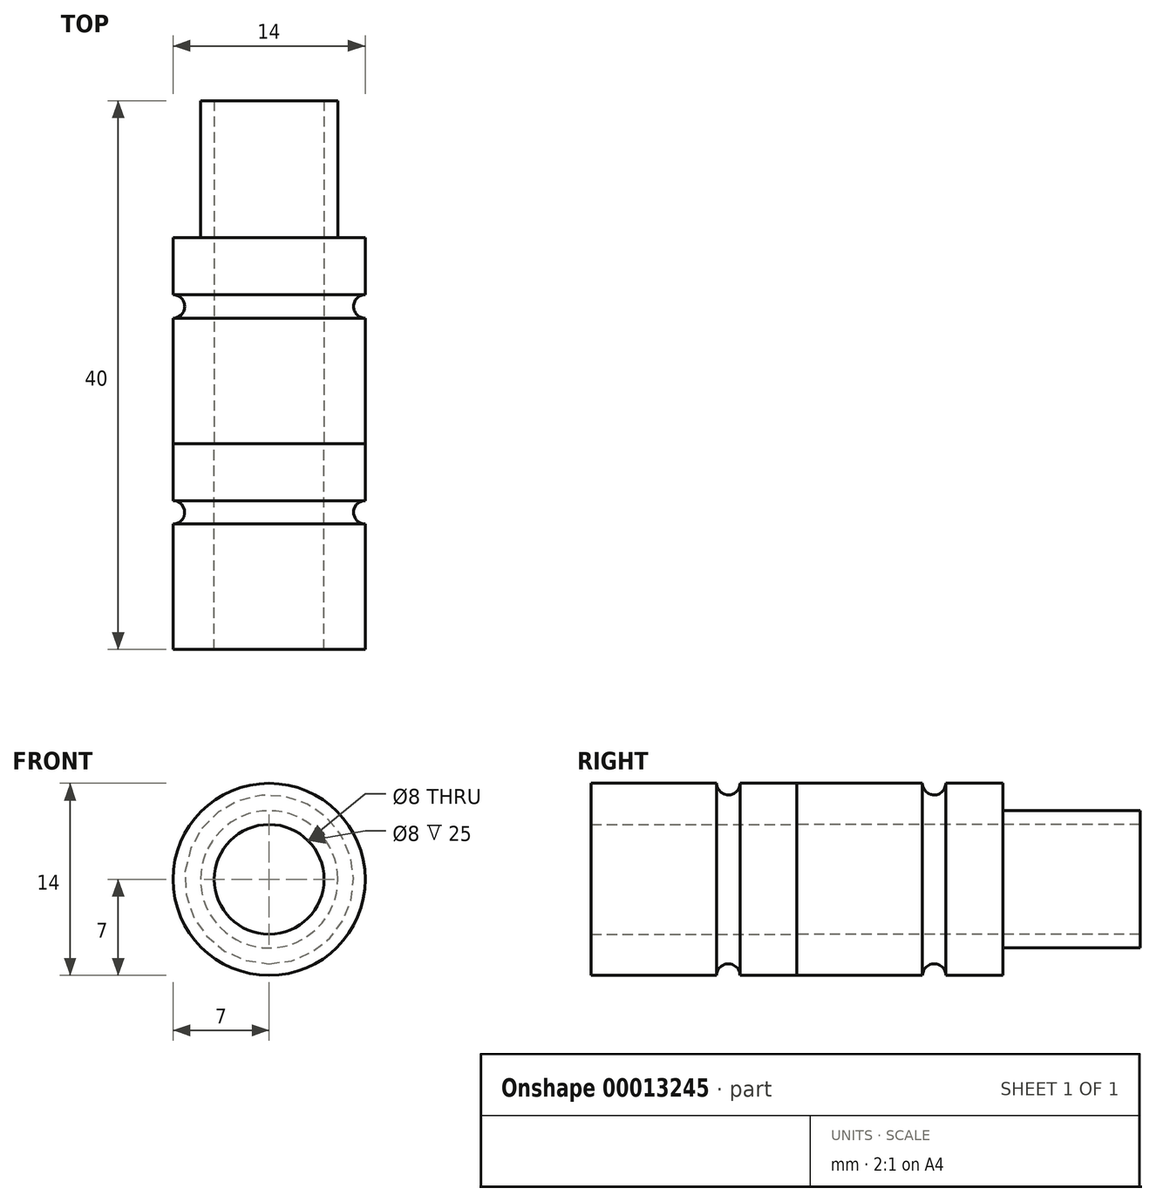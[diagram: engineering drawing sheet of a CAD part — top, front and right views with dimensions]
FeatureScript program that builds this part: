
annotation { "Feature Type Name" : "Feature", "Feature Type Description" : "" }
export const myFeature = defineFeature(function(context is Context, id is Id, definition is map)
    precondition{}
    {
        {
            var Q0;
            Q0=qCreatedBy(makeId("Front.planeOp"),FACE);
            var sketch = newSketch(context, id + "F0", { "sketchPlane" : qUnion([Q0])});
            skCircle(sketch, "E0", {"center": v(0, 0) * mm, "radius": 5 * mm});
            skSolve(sketch);
        }
        {
            var Q0;
            Q0 = qSketchRegion(id + "F0", true);
            extrude(context, id + "F1", {"entities" : qUnion([Q0]), "depth" : 10 * mm});
        }
        {
            var Q0;
            Q0=makeQuery(id+"F1.opExtrude","CAP_FACE",FACE,{"disambiguationData":[OSD([sQuery(id+"F0.wireOp",EDGE,"E0")])],"isStart":false});
            var sketch = newSketch(context, id + "F2", { "sketchPlane" : qUnion([Q0])});
            skCircle(sketch, "E1", {"center": v(0, 0) * mm, "radius": 7 * mm});
            skSolve(sketch);
        }
        {
            var Q0;
            Q0 = qSketchRegion(id + "F2", true);
            extrude(context, id + "F3", {"entities" : qUnion([Q0]), "operationType" : NewBodyOperationType.ADD, "depth" : 15 * mm});
        }
        {
            var Q0;
            Q0=makeQuery(id+"F3.opExtrude","CAP_FACE",FACE,{"disambiguationData":[OSD([sQuery(id+"F2.wireOp",EDGE,"E1")])],"isStart":false});
            var sketch = newSketch(context, id + "F4", { "sketchPlane" : qUnion([Q0])});
            skCircle(sketch, "E2", {"center": v(0, 0) * mm, "radius": 4 * mm});
            skSolve(sketch);
        }
        {
            var Q0;
            Q0 = qSketchRegion(id + "F4", true);
            extrude(context, id + "F5", {"entities" : qUnion([Q0]), "operationType" : NewBodyOperationType.REMOVE, "oppositeDirection" : true, "depth" : 25 * mm});
        }
        {
            var Q0;
            Q0=makeQuery(id+"F3.opExtrude","CAP_FACE",FACE,{"disambiguationData":[OSD([sQuery(id+"F2.wireOp",EDGE,"E1")])],"isStart":false});
            extrude(context, id + "F6", {"entities" : qUnion([Q0]), "depth" : 15 * mm});
        }
        {
            var Q0;
            Q0=qCreatedBy(makeId("Right.planeOp"),FACE);
            var sketch = newSketch(context, id + "F7", { "sketchPlane" : qUnion([Q0])});
            skLineSegment(sketch, "E3.0", {"start": v(-10, -7) * mm, "end": v(-10, 7) * mm, "construction": true});
            skLineSegment(sketch, "E4", {"start": v(-10, 7) * mm, "end": v(-40, 7) * mm, "construction": true});
            skLineSegment(sketch, "E5.0", {"start": v(-40, -7) * mm, "end": v(-40, 7) * mm, "construction": true});
            skArc(sketch, "E6", {"start": v(-15.85, 7) * mm, "mid": v(-15, 6.15) * mm, "end": v(-14.15, 7) * mm});
            skArc(sketch, "E7", {"start": v(-30.85, 7) * mm, "mid": v(-30, 6.15) * mm, "end": v(-29.15, 7) * mm});
            skLineSegment(sketch, "E8", {"start": v(-30.85, 7) * mm, "end": v(-29.15, 7) * mm});
            skLineSegment(sketch, "E9", {"start": v(-15.85, 7) * mm, "end": v(-14.15, 7) * mm});
            skSolve(sketch);
        }
        {
            var Q0;
            Q0 = qSketchRegion(id + "F7", true);
            var Q1;
            Q1=makeQuery(id+"F3.opExtrude","CAP_EDGE",EDGE,{"disambiguationData":[OSD([sQuery(id+"F2.wireOp",EDGE,"E1")])],"isStart":true});
            revolve(context, id + "F8", {"operationType" : NewBodyOperationType.REMOVE, "entities" : qUnion([Q0]), "axis" : qUnion([Q1]), "revolveType" : RevolveType.FULL, "oppositeDirection" : true});
        }
    });
